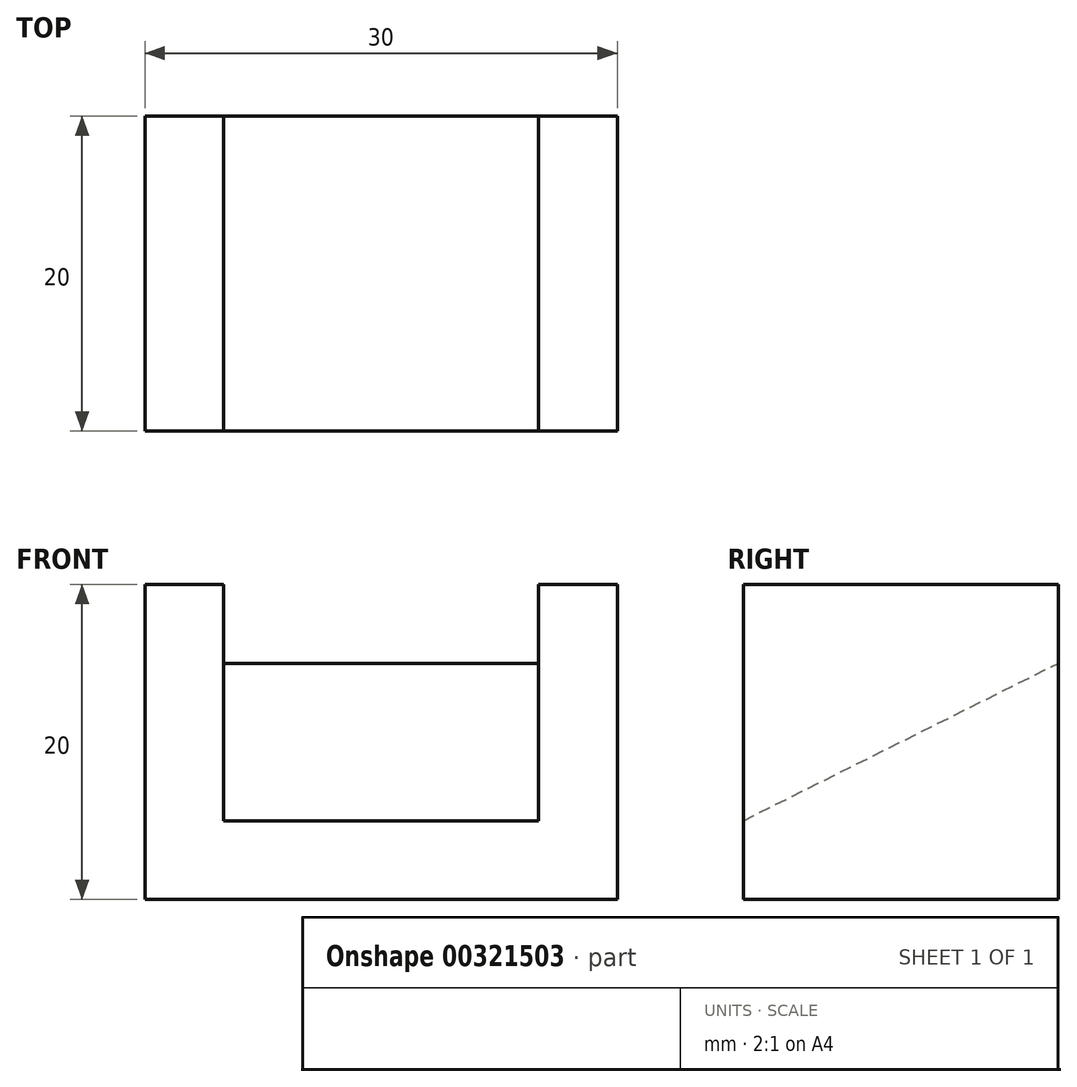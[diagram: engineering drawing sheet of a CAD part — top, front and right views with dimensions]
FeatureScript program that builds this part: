
annotation { "Feature Type Name" : "Feature", "Feature Type Description" : "" }
export const myFeature = defineFeature(function(context is Context, id is Id, definition is map)
    precondition{}
    {
        {
            var Q0;
            Q0=qCreatedBy(makeId("Right.planeOp"),FACE);
            var sketch = newSketch(context, id + "F0", { "sketchPlane" : qUnion([Q0])});
            skLineSegment(sketch, "E0.bottom", {"start": v(0, 0) * mm, "end": v(20, 0) * mm});
            skLineSegment(sketch, "E0.left", {"start": v(0, 0) * mm, "end": v(0, 5) * mm});
            skLineSegment(sketch, "E0.right", {"start": v(20, 0) * mm, "end": v(20, 15) * mm});
            skLineSegment(sketch, "E1", {"start": v(0, 5) * mm, "end": v(20, 15) * mm});
            skSolve(sketch);
        }
        {
            var Q0;
            Q0 = qSketchRegion(id + "F0", true);
            extrude(context, id + "F1", {"entities" : qUnion([Q0]), "endBound" : BoundingType.SYMMETRIC, "depth" : 20 * mm});
        }
        {
            var Q0;
            Q0=makeQuery(id+"F1.opExtrude","CAP_FACE",FACE,{"disambiguationData":[OSD([sQuery(id+"F0.wireOp",EDGE,"E0.bottom"),sQuery(id+"F0.wireOp",EDGE,"E0.left"),sQuery(id+"F0.wireOp",EDGE,"E0.right"),sQuery(id+"F0.wireOp",EDGE,"E1")])],"isStart":false});
            var sketch = newSketch(context, id + "F2", { "sketchPlane" : qUnion([Q0])});
            skLineSegment(sketch, "E2.bottom", {"start": v(20, 0) * mm, "end": v(0, 0) * mm});
            skLineSegment(sketch, "E2.top", {"start": v(20, 20) * mm, "end": v(0, 20) * mm});
            skLineSegment(sketch, "E2.left", {"start": v(20, 0) * mm, "end": v(20, 20) * mm});
            skLineSegment(sketch, "E2.right", {"start": v(0, 0) * mm, "end": v(0, 20) * mm});
            skSolve(sketch);
        }
        {
            var Q0;
            Q0 = qSketchRegion(id + "F2", true);
            extrude(context, id + "F3", {"entities" : qUnion([Q0]), "operationType" : NewBodyOperationType.ADD, "depth" : 5 * mm});
        }
        {
            var Q0;
            Q0=makeQuery(id+"F1.opExtrude","CAP_FACE",FACE,{"disambiguationData":[OSD([sQuery(id+"F0.wireOp",EDGE,"E0.bottom"),sQuery(id+"F0.wireOp",EDGE,"E0.left"),sQuery(id+"F0.wireOp",EDGE,"E0.right"),sQuery(id+"F0.wireOp",EDGE,"E1")])],"isStart":true});
            var sketch = newSketch(context, id + "F4", { "sketchPlane" : qUnion([Q0])});
            skLineSegment(sketch, "E3.bottom", {"start": v(-20, 0) * mm, "end": v(0, 0) * mm});
            skLineSegment(sketch, "E3.top", {"start": v(-20, 20) * mm, "end": v(0, 20) * mm});
            skLineSegment(sketch, "E3.left", {"start": v(-20, 0) * mm, "end": v(-20, 20) * mm});
            skLineSegment(sketch, "E3.right", {"start": v(0, 0) * mm, "end": v(0, 20) * mm});
            skSolve(sketch);
        }
        {
            var Q0;
            Q0 = qSketchRegion(id + "F4", true);
            extrude(context, id + "F5", {"entities" : qUnion([Q0]), "operationType" : NewBodyOperationType.ADD, "depth" : 5 * mm});
        }
    });
